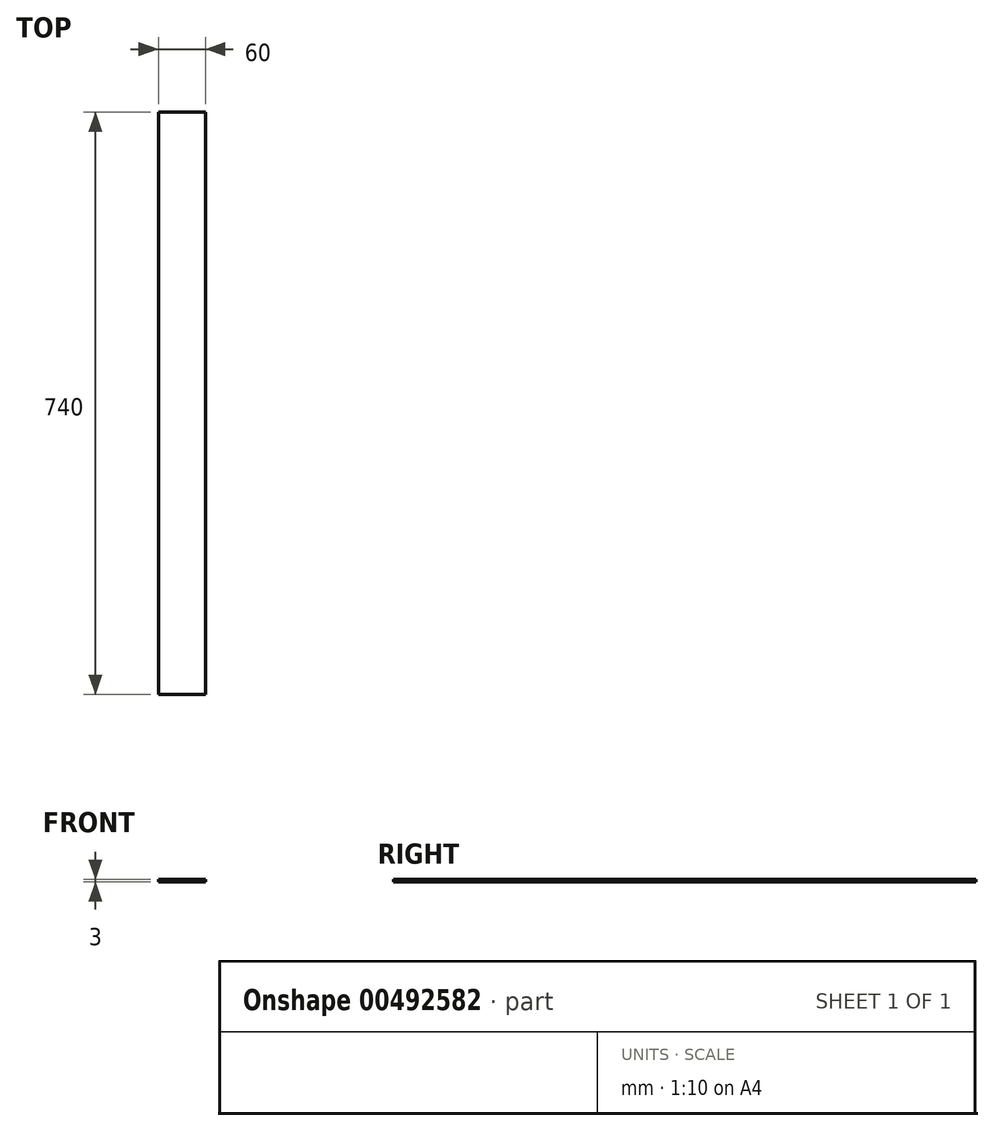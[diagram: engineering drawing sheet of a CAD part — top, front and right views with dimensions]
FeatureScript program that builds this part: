
annotation { "Feature Type Name" : "Feature", "Feature Type Description" : "" }
export const myFeature = defineFeature(function(context is Context, id is Id, definition is map)
    precondition{}
    {
        {
            var Q0;
            Q0=qCreatedBy(makeId("Top.planeOp"),FACE);
            var sketch = newSketch(context, id + "F0", { "sketchPlane" : qUnion([Q0])});
            skLineSegment(sketch, "E0.bottom", {"start": v(-40.15, 467.98) * mm, "end": v(19.85, 467.98) * mm});
            skLineSegment(sketch, "E0.top", {"start": v(-40.15, -272.02) * mm, "end": v(19.85, -272.02) * mm});
            skLineSegment(sketch, "E0.left", {"start": v(-40.15, 467.98) * mm, "end": v(-40.15, -272.02) * mm});
            skLineSegment(sketch, "E0.right", {"start": v(19.85, 467.98) * mm, "end": v(19.85, -272.02) * mm});
            skSolve(sketch);
        }
        {
            var Q0;
            Q0=makeQuery(id+"F0.imprint","IMPRINT",FACE,{"disambiguationData":[TD([[makeQuery(id+"F0.imprint","IMPRINT",EDGE,{"derivedFrom":sQuery(id+"F0.wireOp",EDGE,"E0.bottom")}),-1.0]])]});
            extrude(context, id + "F1", {"entities" : qUnion([Q0]), "depth" : 3 * mm});
        }
    });
